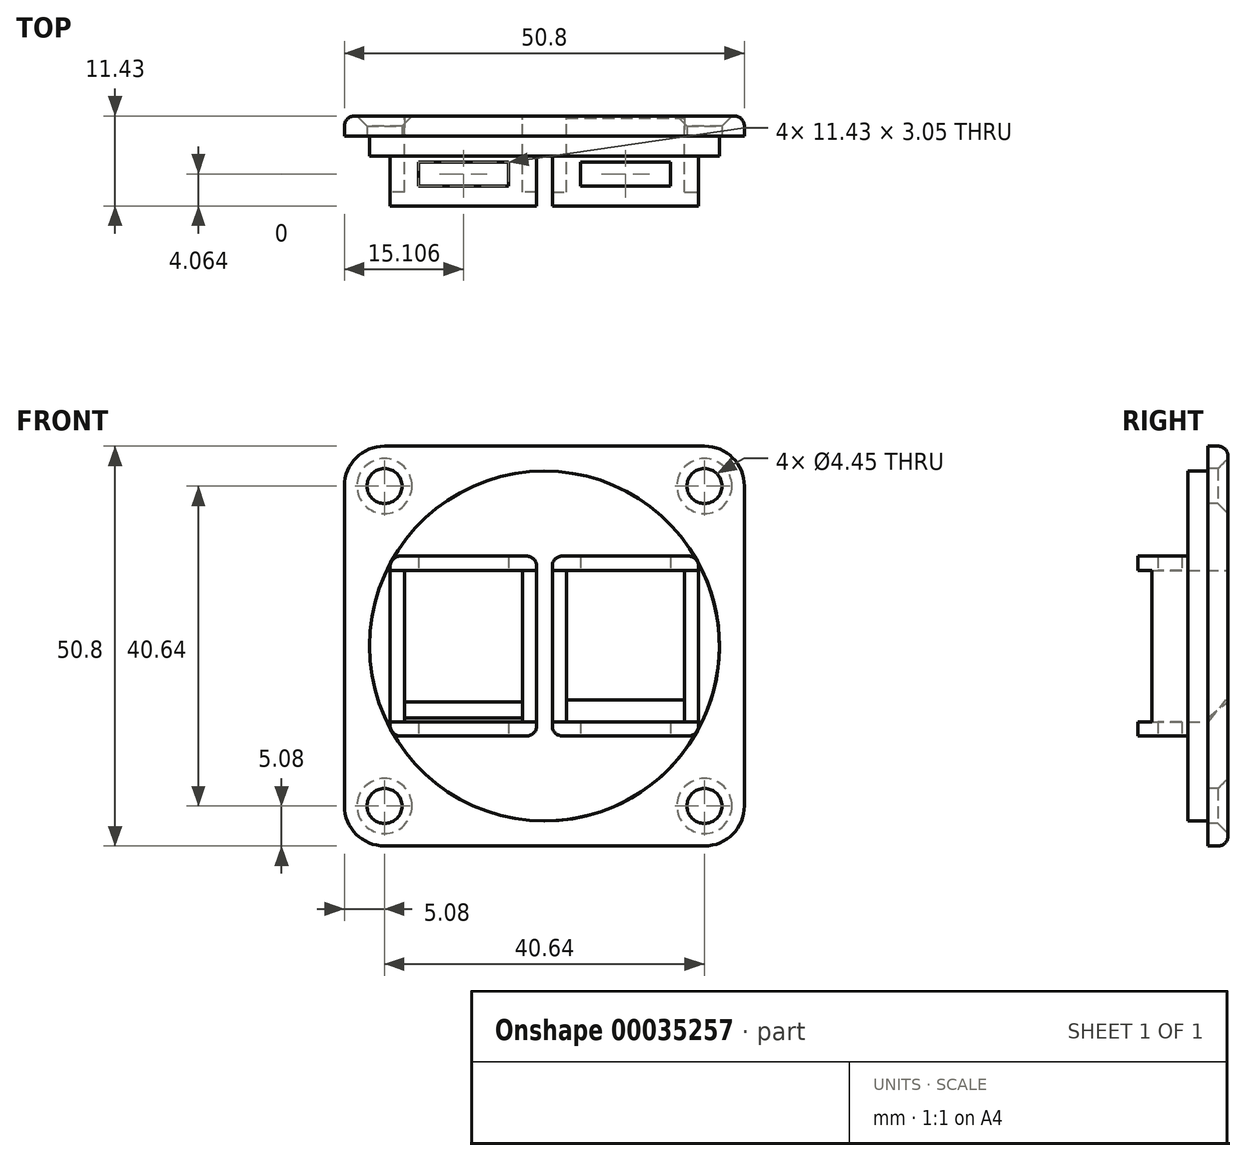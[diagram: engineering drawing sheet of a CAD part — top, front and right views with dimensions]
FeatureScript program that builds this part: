
annotation { "Feature Type Name" : "Feature", "Feature Type Description" : "" }
export const myFeature = defineFeature(function(context is Context, id is Id, definition is map)
    precondition{}
    {
        {
            var Q0;
            Q0=qCreatedBy(makeId("Front.planeOp"),FACE);
            var sketch = newSketch(context, id + "F0", { "sketchPlane" : qUnion([Q0])});
            skCircle(sketch, "E0", {"center": v(0, 0) * mm, "radius": 22.22 * mm});
            skSolve(sketch);
        }
        {
            var Q0;
            Q0=qSketchRegion(id+"F0",true);
            extrude(context, id + "F1", {"entities" : qUnion([Q0]), "depth" : 2.54 * mm});
        }
        {
            var Q0;
            Q0=makeQuery(id+"F1.opExtrude","CAP_FACE",FACE,{"disambiguationData":[OSD([sQuery(id+"F0.wireOp",EDGE,"E0")])],"isStart":true});
            var sketch = newSketch(context, id + "F2", { "sketchPlane" : qUnion([Q0])});
            skLineSegment(sketch, "E1.rect.bottom", {"start": v(20.32, -25.4) * mm, "end": v(-20.32, -25.4) * mm});
            skLineSegment(sketch, "E1.rect.top", {"start": v(20.32, 25.4) * mm, "end": v(-20.32, 25.4) * mm});
            skLineSegment(sketch, "E1.rect.left", {"start": v(25.4, -20.32) * mm, "end": v(25.4, 20.32) * mm});
            skLineSegment(sketch, "E1.rect.right", {"start": v(-25.4, -20.32) * mm, "end": v(-25.4, 20.32) * mm});
            skPoint(sketch, "E1.rect.middle", {"position": v(0, 0) * mm});
            skPoint(sketch, "E2.visualSharp", {"position": v(-25.4, 25.4) * mm});
            skArc(sketch, "E2.filletArc", {"start": v(-20.32, 25.4) * mm, "mid": v(-23.91, 23.91) * mm, "end": v(-25.4, 20.32) * mm});
            skPoint(sketch, "E3.visualSharp", {"position": v(25.4, 25.4) * mm});
            skArc(sketch, "E3.filletArc", {"start": v(25.4, 20.32) * mm, "mid": v(23.91, 23.91) * mm, "end": v(20.32, 25.4) * mm});
            skPoint(sketch, "E4.visualSharp", {"position": v(25.4, -25.4) * mm});
            skArc(sketch, "E4.filletArc", {"start": v(20.32, -25.4) * mm, "mid": v(23.91, -23.91) * mm, "end": v(25.4, -20.32) * mm});
            skPoint(sketch, "E5.visualSharp", {"position": v(-25.4, -25.4) * mm});
            skArc(sketch, "E5.filletArc", {"start": v(-25.4, -20.32) * mm, "mid": v(-23.91, -23.91) * mm, "end": v(-20.32, -25.4) * mm});
            skCircle(sketch, "E6", {"center": v(-20.32, 20.32) * mm, "radius": 2.22 * mm});
            skCircle(sketch, "E7", {"center": v(20.32, 20.32) * mm, "radius": 2.22 * mm});
            skCircle(sketch, "E8", {"center": v(20.32, -20.32) * mm, "radius": 2.22 * mm});
            skCircle(sketch, "E9", {"center": v(-20.32, -20.32) * mm, "radius": 2.22 * mm});
            skSolve(sketch);
        }
        {
            var Q0;
            Q0=qSketchRegion(id+"F2",true);
            extrude(context, id + "F3", {"entities" : qUnion([Q0]), "operationType" : NewBodyOperationType.ADD, "depth" : 2.54 * mm});
        }
        {
            var Q0;
            Q0=makeQuery(id+"F3.opExtrude","CAP_FACE",FACE,{"disambiguationData":[OSD([sQuery(id+"F2.wireOp",EDGE,"E1.rect.bottom"),sQuery(id+"F2.wireOp",EDGE,"E1.rect.top"),sQuery(id+"F2.wireOp",EDGE,"E1.rect.left"),sQuery(id+"F2.wireOp",EDGE,"E1.rect.right"),sQuery(id+"F2.wireOp",EDGE,"E2.filletArc"),sQuery(id+"F2.wireOp",EDGE,"E3.filletArc"),sQuery(id+"F2.wireOp",EDGE,"E4.filletArc"),sQuery(id+"F2.wireOp",EDGE,"E5.filletArc"),sQuery(id+"F2.wireOp",EDGE,"E6"),sQuery(id+"F2.wireOp",EDGE,"E7"),sQuery(id+"F2.wireOp",EDGE,"E8"),sQuery(id+"F2.wireOp",EDGE,"E9")])],"isStart":false});
            var sketch = newSketch(context, id + "F4", { "sketchPlane" : qUnion([Q0])});
            skLineSegment(sketch, "E10.rect.bottom", {"start": v(-2.8, -9.63) * mm, "end": v(-17.8, -9.62) * mm});
            skLineSegment(sketch, "E10.rect.top", {"start": v(-2.8, 9.62) * mm, "end": v(-17.8, 9.63) * mm});
            skLineSegment(sketch, "E10.rect.left", {"start": v(-2.8, -9.63) * mm, "end": v(-2.8, 9.62) * mm});
            skLineSegment(sketch, "E10.rect.right", {"start": v(-17.8, -9.62) * mm, "end": v(-17.8, 9.63) * mm});
            skPoint(sketch, "E10.rect.middle", {"position": v(-10.3, 0) * mm});
            skLineSegment(sketch, "E11", {"start": v(0, 25.4) * mm, "end": v(0, -25.4) * mm, "construction": true});
            skLineSegment(sketch, "E12.MirrorCS", {"start": v(2.8, -9.63) * mm, "end": v(17.8, -9.63) * mm});
            skLineSegment(sketch, "E13.MirrorCS", {"start": v(2.8, -9.62) * mm, "end": v(2.8, 9.62) * mm});
            skLineSegment(sketch, "E14.MirrorCS", {"start": v(2.8, 9.62) * mm, "end": v(17.8, 9.62) * mm});
            skLineSegment(sketch, "E15.MirrorCS", {"start": v(17.8, -9.62) * mm, "end": v(17.8, 9.63) * mm});
            skSolve(sketch);
        }
        {
            var Q0;
            Q0=qSketchRegion(id+"F4",true);
            extrude(context, id + "F5", {"entities" : qUnion([Q0]), "operationType" : NewBodyOperationType.REMOVE, "endBound" : BoundingType.THROUGH_ALL, "oppositeDirection" : true, "depth" : 25.4 * mm});
        }
        {
            var Q0;
            Q0=makeQuery(id+"F1.opExtrude","CAP_FACE",FACE,{"disambiguationData":[OSD([sQuery(id+"F0.wireOp",EDGE,"E0")])],"isStart":false});
            var sketch = newSketch(context, id + "F6", { "sketchPlane" : qUnion([Q0])});
            skLineSegment(sketch, "E16.0", {"start": v(18.32, 11.42) * mm, "end": v(2.26, 11.42) * mm});
            skLineSegment(sketch, "E16.1", {"start": v(19.6, 10.15) * mm, "end": v(19.6, -10.16) * mm});
            skLineSegment(sketch, "E16.2", {"start": v(18.32, -11.43) * mm, "end": v(2.26, -11.43) * mm});
            skLineSegment(sketch, "E16.3", {"start": v(1, 10.15) * mm, "end": v(1, -10.16) * mm});
            skLineSegment(sketch, "E17.0", {"start": v(17.8, 9.62) * mm, "end": v(2.8, 9.62) * mm});
            skLineSegment(sketch, "E17.1", {"start": v(17.8, 9.62) * mm, "end": v(17.8, -9.62) * mm});
            skLineSegment(sketch, "E17.2", {"start": v(17.8, -9.63) * mm, "end": v(2.8, -9.63) * mm});
            skLineSegment(sketch, "E17.3", {"start": v(2.8, 9.62) * mm, "end": v(2.8, -9.62) * mm});
            skPoint(sketch, "E18.visualSharp", {"position": v(1, 11.42) * mm});
            skArc(sketch, "E18.filletArc", {"start": v(2.26, 11.42) * mm, "mid": v(1.37, 11.05) * mm, "end": v(1, 10.15) * mm});
            skPoint(sketch, "E19.visualSharp", {"position": v(19.6, 11.42) * mm});
            skArc(sketch, "E19.filletArc", {"start": v(19.6, 10.15) * mm, "mid": v(19.22, 11.05) * mm, "end": v(18.32, 11.42) * mm});
            skPoint(sketch, "E20.visualSharp", {"position": v(19.6, -11.43) * mm});
            skArc(sketch, "E20.filletArc", {"start": v(18.32, -11.43) * mm, "mid": v(19.22, -11.05) * mm, "end": v(19.6, -10.16) * mm});
            skPoint(sketch, "E21.visualSharp", {"position": v(1, -11.43) * mm});
            skArc(sketch, "E21.filletArc", {"start": v(1, -10.16) * mm, "mid": v(1.37, -11.05) * mm, "end": v(2.26, -11.43) * mm});
            skLineSegment(sketch, "E22", {"start": v(0, 22.22) * mm, "end": v(0, -22.22) * mm, "construction": true});
            skLineSegment(sketch, "E23.MirrorCS", {"start": v(-18.32, 11.42) * mm, "end": v(-2.26, 11.42) * mm});
            skArc(sketch, "E24.MirrorCS", {"start": v(-2.26, 11.42) * mm, "mid": v(-1.37, 11.05) * mm, "end": v(-1, 10.15) * mm});
            skLineSegment(sketch, "E25.MirrorCS", {"start": v(-1, 10.15) * mm, "end": v(-1, -10.16) * mm});
            skArc(sketch, "E26.MirrorCS", {"start": v(-1, -10.16) * mm, "mid": v(-1.37, -11.05) * mm, "end": v(-2.26, -11.43) * mm});
            skLineSegment(sketch, "E27.MirrorCS", {"start": v(-18.32, -11.43) * mm, "end": v(-2.26, -11.43) * mm});
            skArc(sketch, "E28.MirrorCS", {"start": v(-18.32, -11.43) * mm, "mid": v(-19.22, -11.05) * mm, "end": v(-19.6, -10.16) * mm});
            skLineSegment(sketch, "E29.MirrorCS", {"start": v(-19.6, 10.15) * mm, "end": v(-19.6, -10.16) * mm});
            skArc(sketch, "E30.MirrorCS", {"start": v(-19.6, 10.15) * mm, "mid": v(-19.22, 11.05) * mm, "end": v(-18.32, 11.42) * mm});
            skLineSegment(sketch, "E31.MirrorCS", {"start": v(-17.8, 9.62) * mm, "end": v(-2.8, 9.62) * mm});
            skLineSegment(sketch, "E32.MirrorCS", {"start": v(-17.8, 9.62) * mm, "end": v(-17.8, -9.63) * mm});
            skLineSegment(sketch, "E33.MirrorCS", {"start": v(-17.8, -9.63) * mm, "end": v(-2.8, -9.63) * mm});
            skLineSegment(sketch, "E34.MirrorCS", {"start": v(-2.8, 9.62) * mm, "end": v(-2.8, -9.62) * mm});
            skSolve(sketch);
        }
        {
            var Q0;
            Q0=qSketchRegion(id+"F6",true);
            extrude(context, id + "F7", {"entities" : qUnion([Q0]), "operationType" : NewBodyOperationType.ADD, "depth" : 6.35 * mm});
        }
        {
            var Q0;
            Q0=makeQuery(id+"F7.opExtrude","SWEPT_FACE",FACE,{"disambiguationData":[OSD([sQuery(id+"F6.wireOp",EDGE,"E16.2")])]});
            var sketch = newSketch(context, id + "F8", { "sketchPlane" : qUnion([Q0])});
            skLineSegment(sketch, "E35", {"start": v(10.3, 8.9) * mm, "end": v(10.3, 2.54) * mm, "construction": true});
            skLineSegment(sketch, "E36.rect.bottom", {"start": v(16, 3.3) * mm, "end": v(4.58, 3.3) * mm});
            skLineSegment(sketch, "E36.rect.top", {"start": v(16, 6.35) * mm, "end": v(4.58, 6.35) * mm});
            skLineSegment(sketch, "E36.rect.left", {"start": v(16, 3.3) * mm, "end": v(16, 6.35) * mm});
            skLineSegment(sketch, "E36.rect.right", {"start": v(4.58, 3.3) * mm, "end": v(4.58, 6.35) * mm});
            skPoint(sketch, "E36.rect.middle", {"position": v(10.3, 4.83) * mm});
            skLineSegment(sketch, "E37.MirrorCS", {"start": v(-16, 6.35) * mm, "end": v(-4.58, 6.35) * mm});
            skLineSegment(sketch, "E38.MirrorCS", {"start": v(-4.58, 3.3) * mm, "end": v(-4.58, 6.35) * mm});
            skLineSegment(sketch, "E39.MirrorCS", {"start": v(-16, 3.3) * mm, "end": v(-4.58, 3.3) * mm});
            skLineSegment(sketch, "E40.MirrorCS", {"start": v(-16, 3.3) * mm, "end": v(-16, 6.35) * mm});
            skSolve(sketch);
        }
        {
            var Q0;
            Q0=qSketchRegion(id+"F8",true);
            extrude(context, id + "F9", {"entities" : qUnion([Q0]), "operationType" : NewBodyOperationType.REMOVE, "endBound" : BoundingType.THROUGH_ALL, "oppositeDirection" : true, "depth" : 25.4 * mm});
        }
        {
            var Q0;
            Q0=makeQuery(id+"F7.opExtrude","CAP_FACE",FACE,{"disambiguationData":[OSD([sQuery(id+"F6.wireOp",EDGE,"E16.0"),sQuery(id+"F6.wireOp",EDGE,"E16.1"),sQuery(id+"F6.wireOp",EDGE,"E16.2"),sQuery(id+"F6.wireOp",EDGE,"E16.3"),sQuery(id+"F6.wireOp",EDGE,"E17.0"),sQuery(id+"F6.wireOp",EDGE,"E17.1"),sQuery(id+"F6.wireOp",EDGE,"E17.2"),sQuery(id+"F6.wireOp",EDGE,"E17.3"),sQuery(id+"F6.wireOp",EDGE,"E18.filletArc"),sQuery(id+"F6.wireOp",EDGE,"E19.filletArc"),sQuery(id+"F6.wireOp",EDGE,"E20.filletArc"),sQuery(id+"F6.wireOp",EDGE,"E21.filletArc")])],"isStart":false});
            var sketch = newSketch(context, id + "F10", { "sketchPlane" : qUnion([Q0])});
            skLineSegment(sketch, "E41.bottom", {"start": v(1, 9.62) * mm, "end": v(19.6, 9.62) * mm});
            skLineSegment(sketch, "E41.top", {"start": v(1, -9.63) * mm, "end": v(19.6, -9.63) * mm});
            skLineSegment(sketch, "E41.left", {"start": v(1, 9.62) * mm, "end": v(1, -9.62) * mm});
            skLineSegment(sketch, "E41.right", {"start": v(19.6, 9.62) * mm, "end": v(19.6, -9.63) * mm});
            skLineSegment(sketch, "E42.MirrorCS", {"start": v(-1, 9.62) * mm, "end": v(-19.6, 9.62) * mm});
            skLineSegment(sketch, "E43.MirrorCS", {"start": v(-1, 9.62) * mm, "end": v(-1, -9.62) * mm});
            skLineSegment(sketch, "E44.MirrorCS", {"start": v(-1, -9.62) * mm, "end": v(-19.6, -9.63) * mm});
            skLineSegment(sketch, "E45.MirrorCS", {"start": v(-19.6, 9.62) * mm, "end": v(-19.6, -9.63) * mm});
            skSolve(sketch);
        }
        {
            var Q0;
            Q0=qSketchRegion(id+"F10",true);
            extrude(context, id + "F11", {"entities" : qUnion([Q0]), "operationType" : NewBodyOperationType.REMOVE, "oppositeDirection" : true, "depth" : 1.78 * mm});
        }
        {
            var Q0;
            Q0=makeQuery(id+"F3.opExtrude","CAP_FACE",FACE,{"disambiguationData":[OSD([sQuery(id+"F2.wireOp",EDGE,"E1.rect.bottom"),sQuery(id+"F2.wireOp",EDGE,"E1.rect.top"),sQuery(id+"F2.wireOp",EDGE,"E1.rect.left"),sQuery(id+"F2.wireOp",EDGE,"E1.rect.right"),sQuery(id+"F2.wireOp",EDGE,"E2.filletArc"),sQuery(id+"F2.wireOp",EDGE,"E3.filletArc"),sQuery(id+"F2.wireOp",EDGE,"E4.filletArc"),sQuery(id+"F2.wireOp",EDGE,"E5.filletArc"),sQuery(id+"F2.wireOp",EDGE,"E6"),sQuery(id+"F2.wireOp",EDGE,"E7"),sQuery(id+"F2.wireOp",EDGE,"E8"),sQuery(id+"F2.wireOp",EDGE,"E9")])],"isStart":false});
            var sketch = newSketch(context, id + "F12", { "sketchPlane" : qUnion([Q0])});
            skLineSegment(sketch, "E46.bottom", {"start": v(-2.8, -9.63) * mm, "end": v(-17.8, -9.63) * mm});
            skLineSegment(sketch, "E46.top", {"start": v(-2.8, -6.88) * mm, "end": v(-17.8, -6.87) * mm});
            skLineSegment(sketch, "E46.left", {"start": v(-2.8, -9.63) * mm, "end": v(-2.8, -6.88) * mm});
            skLineSegment(sketch, "E46.right", {"start": v(-17.8, -9.63) * mm, "end": v(-17.8, -6.87) * mm});
            skLineSegment(sketch, "E47.MirrorCS", {"start": v(2.8, -6.88) * mm, "end": v(17.8, -6.88) * mm});
            skLineSegment(sketch, "E48.MirrorCS", {"start": v(17.8, -9.63) * mm, "end": v(17.8, -6.87) * mm});
            skLineSegment(sketch, "E49.MirrorCS", {"start": v(2.8, -9.63) * mm, "end": v(17.8, -9.62) * mm});
            skLineSegment(sketch, "E50.MirrorCS", {"start": v(2.8, -9.63) * mm, "end": v(2.8, -6.88) * mm});
            skSolve(sketch);
        }
        {
            var Q0;
            Q0=qSketchRegion(id+"F12",true);
            extrude(context, id + "F13", {"entities" : qUnion([Q0]), "operationType" : NewBodyOperationType.ADD, "oppositeDirection" : true, "depth" : 2.54 * mm});
        }
        {
            var Q0;
            Q0=makeQuery(id+"F3.opExtrude","CAP_EDGE",EDGE,{"disambiguationData":[OSD([sQuery(id+"F2.wireOp",EDGE,"E6")])],"isStart":false});
            var Q1;
            Q1=makeQuery(id+"F3.opExtrude","CAP_EDGE",EDGE,{"disambiguationData":[OSD([sQuery(id+"F2.wireOp",EDGE,"E9")])],"isStart":false});
            var Q2;
            Q2=makeQuery(id+"F3.opExtrude","CAP_EDGE",EDGE,{"disambiguationData":[OSD([sQuery(id+"F2.wireOp",EDGE,"E8")])],"isStart":false});
            var Q3;
            Q3=makeQuery(id+"F3.opExtrude","CAP_EDGE",EDGE,{"disambiguationData":[OSD([sQuery(id+"F2.wireOp",EDGE,"E7")])],"isStart":false});
            chamfer(context, id + "F14", {"entities" : qUnion([Q0, Q1, Q2, Q3]), "width" : 1.27 * mm, "tangentPropagation" : true});
        }
        {
            var Q0;
            Q0=makeQuery(id+"F3.opExtrude","CAP_EDGE",EDGE,{"disambiguationData":[OSD([sQuery(id+"F2.wireOp",EDGE,"E1.rect.bottom")])],"isStart":false});
            fillet(context, id + "F15", {"entities" : qUnion([Q0]), "radius" : 1.27 * mm, "tangentPropagation" : true, "allowEdgeOverflow" : false});
        }
        {
            var Q0;
            Q0=makeQuery(id+"F13.opExtrude","CAP_EDGE",EDGE,{"disambiguationData":[OSD([sQuery(id+"F12.wireOp",EDGE,"E47.MirrorCS")])],"isStart":false});
            var Q1;
            Q1=makeQuery(id+"F13.opExtrude","CAP_EDGE",EDGE,{"disambiguationData":[OSD([sQuery(id+"F12.wireOp",EDGE,"E46.top")])],"isStart":false});
            chamfer(context, id + "F16", {"entities" : qUnion([Q0, Q1]), "chamferType" : ChamferType.TWO_OFFSETS, "width1" : 2.3 * mm, "oppositeDirection" : false, "width2" : 2.8 * mm, "tangentPropagation" : true});
        }
    });
